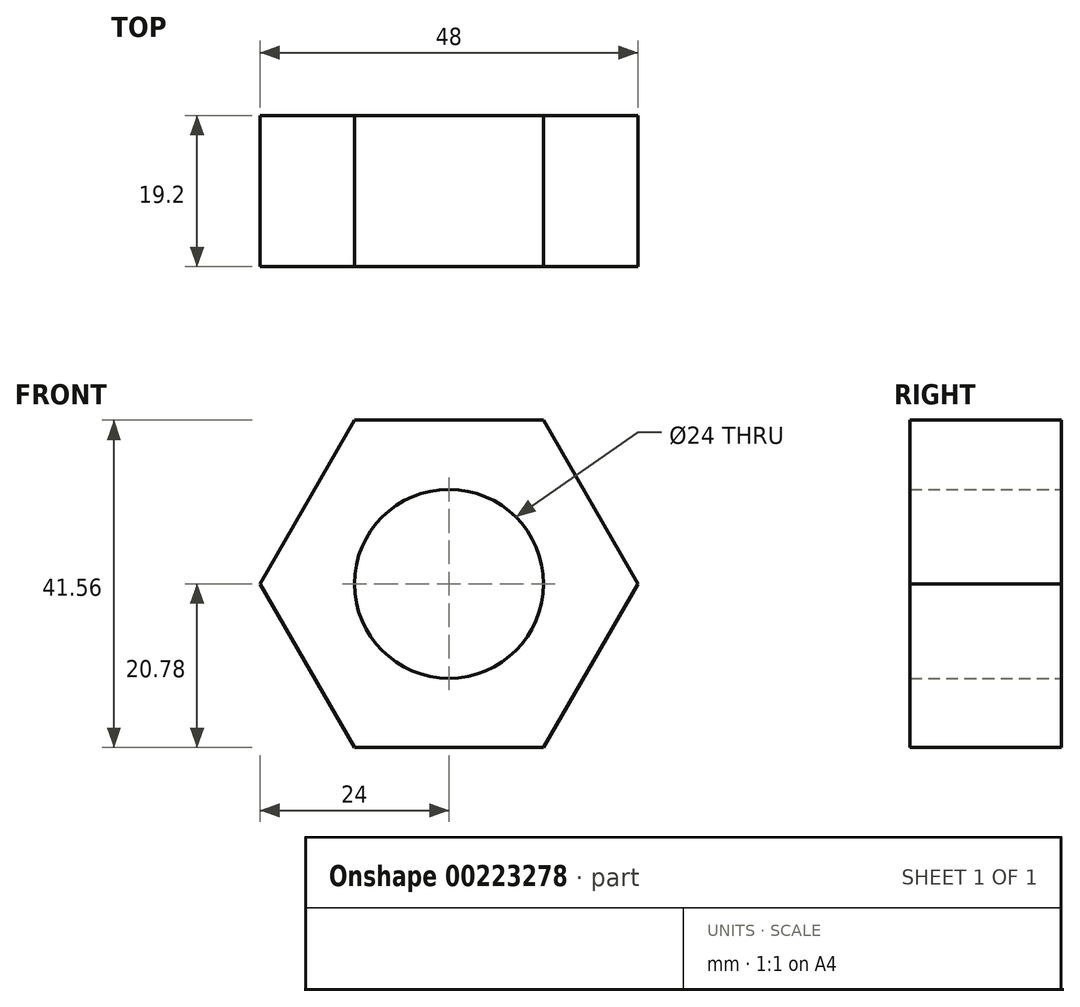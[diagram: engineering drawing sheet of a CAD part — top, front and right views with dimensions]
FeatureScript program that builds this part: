
annotation { "Feature Type Name" : "Feature", "Feature Type Description" : "" }
export const myFeature = defineFeature(function(context is Context, id is Id, definition is map)
    precondition{}
    {
        {
            var Q0;
            Q0=qCreatedBy(makeId("Front.planeOp"),FACE);
            var sketch = newSketch(context, id + "F0", { "sketchPlane" : qUnion([Q0])});
            skCircle(sketch, "E0.cCircle", {"center": v(0, 0) * mm, "radius": 20.78 * mm, "construction": true});
            skLineSegment(sketch, "E0.0", {"start": v(-24, 0) * mm, "end": v(-12, 20.78) * mm});
            skLineSegment(sketch, "E0.1", {"start": v(-12, 20.78) * mm, "end": v(12, 20.78) * mm});
            skLineSegment(sketch, "E0.2", {"start": v(12, 20.78) * mm, "end": v(24, 0) * mm});
            skLineSegment(sketch, "E0.3", {"start": v(24, 0) * mm, "end": v(12, -20.78) * mm});
            skLineSegment(sketch, "E0.4", {"start": v(12, -20.78) * mm, "end": v(-12, -20.78) * mm});
            skLineSegment(sketch, "E0.5", {"start": v(-12, -20.78) * mm, "end": v(-24, 0) * mm});
            skPoint(sketch, "E0.0.midPoint", {"position": v(-18, 10.4) * mm});
            skCircle(sketch, "E1", {"center": v(0, 0) * mm, "radius": 12 * mm});
            skSolve(sketch);
        }
        {
            var Q0;
            Q0=makeQuery(id+"F0.imprint","IMPRINT",FACE,{"disambiguationData":[TD([[makeQuery(id+"F0.imprint","IMPRINT",EDGE,{"derivedFrom":sQuery(id+"F0.wireOp",EDGE,"E0.0")}),-1.0]])]});
            extrude(context, id + "F1", {"entities" : qUnion([Q0]), "depth" : 0.8 * 24 * mm});
        }
    });
